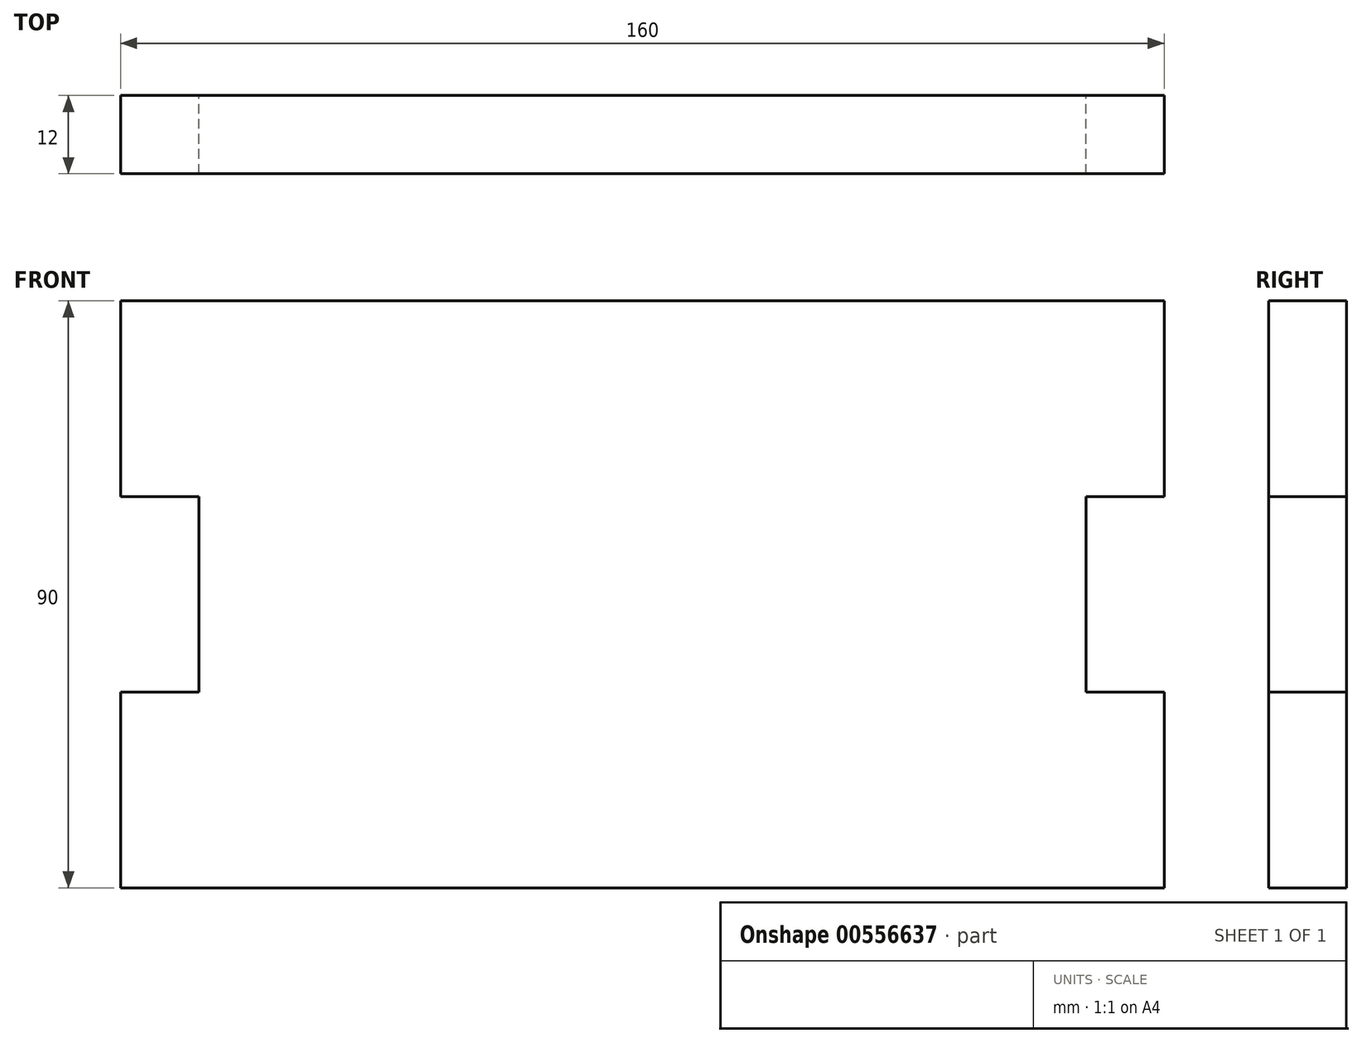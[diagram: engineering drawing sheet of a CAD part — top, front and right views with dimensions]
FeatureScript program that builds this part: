
annotation { "Feature Type Name" : "Feature", "Feature Type Description" : "" }
export const myFeature = defineFeature(function(context is Context, id is Id, definition is map)
    precondition{}
    {
        {
            var Q0;
            Q0=qCreatedBy(makeId("Front.planeOp"),FACE);
            var sketch = newSketch(context, id + "F0", { "sketchPlane" : qUnion([Q0])});
            skLineSegment(sketch, "E0", {"start": v(0, 0) * mm, "end": v(0, 30) * mm});
            skLineSegment(sketch, "E1", {"start": v(0, 30) * mm, "end": v(12, 30) * mm});
            skLineSegment(sketch, "E2", {"start": v(12, 30) * mm, "end": v(12, 60) * mm});
            skLineSegment(sketch, "E3", {"start": v(12, 60) * mm, "end": v(0, 60) * mm});
            skLineSegment(sketch, "E4", {"start": v(0, 60) * mm, "end": v(0, 90) * mm});
            skLineSegment(sketch, "E5", {"start": v(0, 90) * mm, "end": v(80, 90) * mm});
            skLineSegment(sketch, "E6", {"start": v(80, 90) * mm, "end": v(80, 0) * mm, "construction": true});
            skLineSegment(sketch, "E7", {"start": v(80, 0) * mm, "end": v(0, 0) * mm});
            skLineSegment(sketch, "E8.MirrorCS", {"start": v(160, 30) * mm, "end": v(148, 30) * mm});
            skLineSegment(sketch, "E9.MirrorCS", {"start": v(148, 30) * mm, "end": v(148, 60) * mm});
            skLineSegment(sketch, "E10.MirrorCS", {"start": v(160, 60) * mm, "end": v(160, 90) * mm});
            skLineSegment(sketch, "E11.MirrorCS", {"start": v(160, 0) * mm, "end": v(160, 30) * mm});
            skLineSegment(sketch, "E12.MirrorCS", {"start": v(160, 90) * mm, "end": v(80, 90) * mm});
            skLineSegment(sketch, "E13.MirrorCS", {"start": v(148, 60) * mm, "end": v(160, 60) * mm});
            skLineSegment(sketch, "E14.MirrorCS", {"start": v(80, 0) * mm, "end": v(160, 0) * mm});
            skSolve(sketch);
        }
        {
            var Q0;
            Q0 = qSketchRegion(id + "F0", true);
            extrude(context, id + "F1", {"entities" : qUnion([Q0]), "depth" : 12 * mm, "offsetDistance" : 25 * mm});
        }
    });
